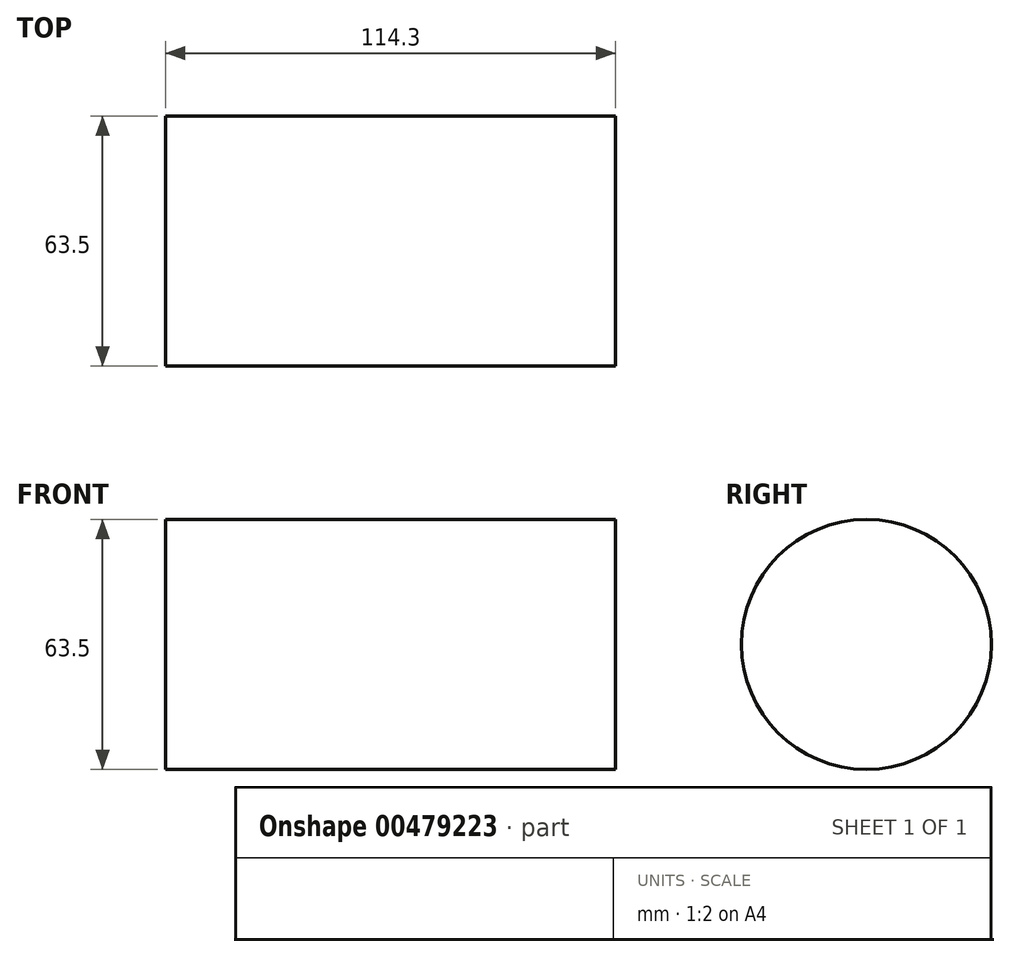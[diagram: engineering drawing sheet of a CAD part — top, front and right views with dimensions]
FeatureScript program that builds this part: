
annotation { "Feature Type Name" : "Feature", "Feature Type Description" : "" }
export const myFeature = defineFeature(function(context is Context, id is Id, definition is map)
    precondition{}
    {
        {
            var Q0;
            Q0=qCreatedBy(makeId("Front.planeOp"),FACE);
            var sketch = newSketch(context, id + "F0", { "sketchPlane" : qUnion([Q0])});
            skLineSegment(sketch, "E0.bottom", {"start": v(-56.2, 37.45) * mm, "end": v(58.1, 37.45) * mm});
            skLineSegment(sketch, "E0.top", {"start": v(-56.2, -26.05) * mm, "end": v(58.1, -26.05) * mm});
            skLineSegment(sketch, "E0.left", {"start": v(-56.2, 37.45) * mm, "end": v(-56.2, -26.05) * mm});
            skLineSegment(sketch, "E0.right", {"start": v(58.1, 37.45) * mm, "end": v(58.1, -26.05) * mm});
            skLineSegment(sketch, "E1", {"start": v(-56.2, 5.7) * mm, "end": v(58.1, 5.7) * mm});
            skSolve(sketch);
        }
        {
            var Q0;
            {var subQ0=sQuery(id+"F0.wireOp",EDGE,"E0.bottom");Q0=makeQuery(id+"F0.imprint","IMPRINT",FACE,{"disambiguationData":[TD([[makeQuery(id+"F0.imprint","IMPRINT",EDGE,{"derivedFrom":subQ0}),-1.0]])]});}
            var Q1;
            Q1=sQuery(id+"F0.wireOp",EDGE,"E1");
            revolve(context, id + "F1", {"entities" : qUnion([Q0]), "axis" : qUnion([Q1]), "revolveType" : RevolveType.FULL});
        }
    });
